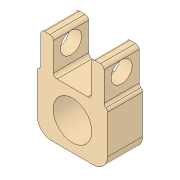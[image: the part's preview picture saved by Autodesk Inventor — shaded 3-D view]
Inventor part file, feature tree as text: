
AUTODESK INVENTOR PART (.ipt)
format: ipt  version: 2018.3 (Build 223284000, 284)  size: 149,504 bytes
history: native  units: in
note: dims shown in document units (in); Inventor stores cm internally (conversion verified against a paired STEP export)
features: extrude x3, fillet x3, sketch x3
ambient origin geometry x8: Origin, YZ Plane, XZ Plane, XY Plane, X Axis, Y Axis, Z Axis, Center Point
bodies: Solid1 (feature_tree)
feature tree (9):
  extrude  "Extrusion1"  Depth=0.625in TaperAngle=0.0deg
  extrude  "Extrusion2"  Depth=0.625in TaperAngle=0.0deg
  extrude  "Extrusion3"  Depth=0.625in TaperAngle=0.0deg
  fillet  "Fillet1"  Radius=0.0625in
  fillet  "Fillet2"  Radius=0.0625in
  fillet  "Fillet3"  Radius=0.25in
  sketch  "Sketch1"  dims[d0=1.0in d1=0.225in d2=0.225in d3=0.625in d4=1.25in d5=0.0625in d6=0.0625in d7=0.675in d8=0.625in d9=0.0in]
  sketch  "Sketch2"  dims[d10=0.6885in d13=0.5in d14=0.625in d15=0.0in]
  sketch  "Sketch3"  dims[d16=0.375in d17=0.25in d18=0.0in d19=0.625in d20=0.0in d21=0.0625in d22=0.0625in d23=0.25in]
